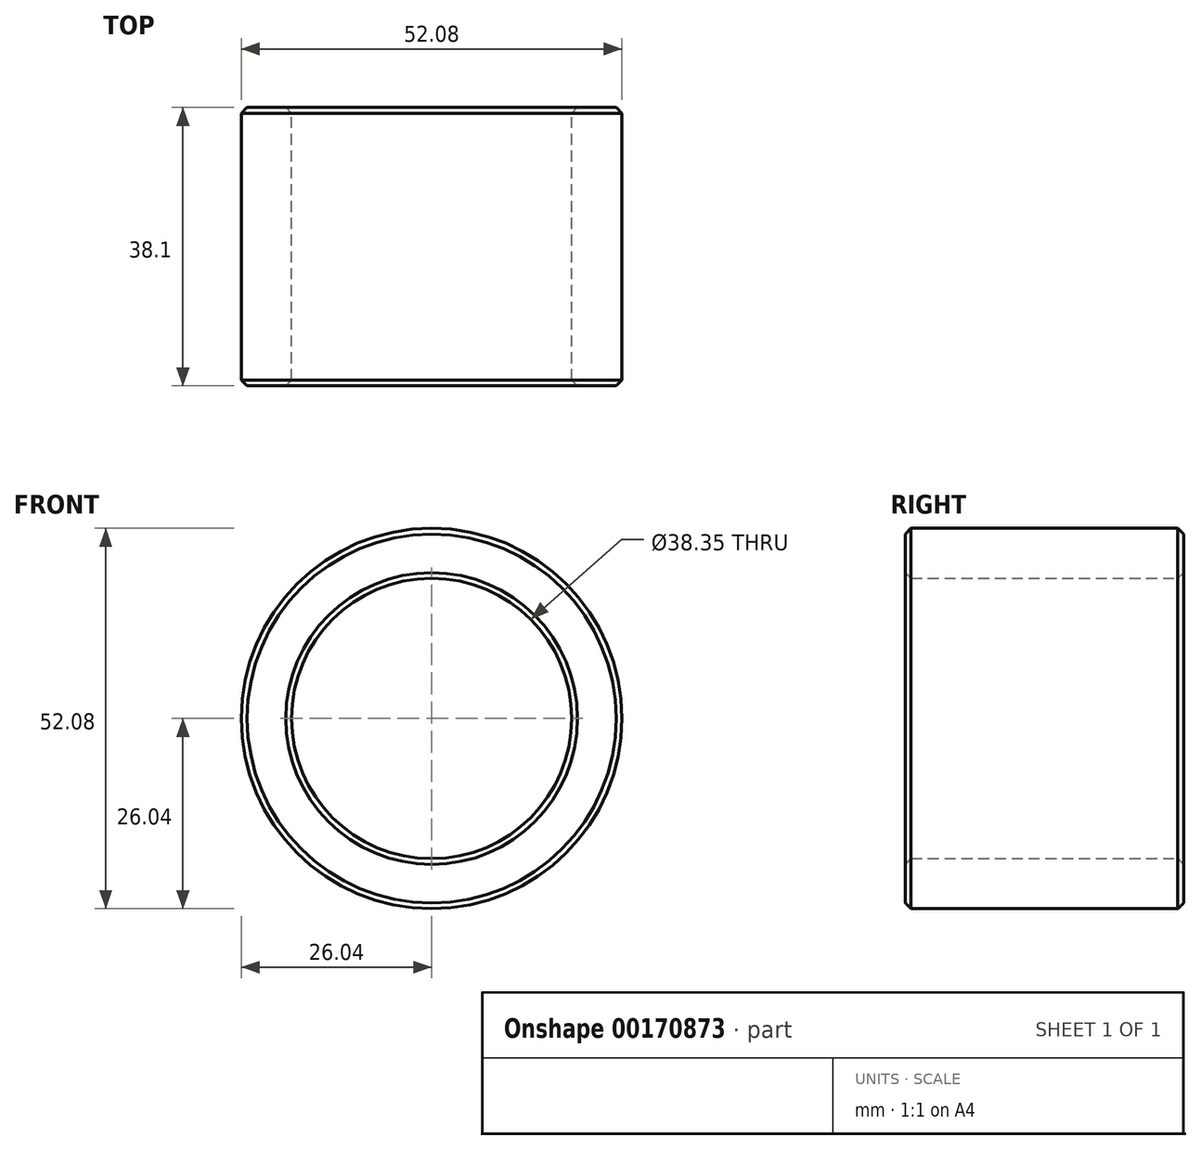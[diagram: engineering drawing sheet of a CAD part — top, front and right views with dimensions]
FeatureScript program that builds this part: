
annotation { "Feature Type Name" : "Feature", "Feature Type Description" : "" }
export const myFeature = defineFeature(function(context is Context, id is Id, definition is map)
    precondition{}
    {
        {
            var Q0;
            Q0=qCreatedBy(makeId("Front.planeOp"),FACE);
            var sketch = newSketch(context, id + "F0", { "sketchPlane" : qUnion([Q0])});
            skCircle(sketch, "E0", {"center": v(0, 0) * mm, "radius": 19.18 * mm});
            skCircle(sketch, "E1", {"center": v(0, 0) * mm, "radius": 26.04 * mm});
            skSolve(sketch);
        }
        {
            var Q0;
            Q0 = qSketchRegion(id + "F0", true);
            extrude(context, id + "F1", {"entities" : qUnion([Q0]), "depth" : 38.1 * mm});
        }
        {
            var Q0;
            Q0=makeQuery(id+"F1.opExtrude","CAP_EDGE",EDGE,{"disambiguationData":[OSD([sQuery(id+"F0.wireOp",EDGE,"E0")])],"isStart":false});
            var Q1;
            Q1=makeQuery(id+"F1.opExtrude","CAP_EDGE",EDGE,{"disambiguationData":[OSD([sQuery(id+"F0.wireOp",EDGE,"E1")])],"isStart":false});
            var Q2;
            Q2=makeQuery(id+"F1.opExtrude","CAP_EDGE",EDGE,{"disambiguationData":[OSD([sQuery(id+"F0.wireOp",EDGE,"E1")])],"isStart":true});
            var Q3;
            Q3=makeQuery(id+"F1.opExtrude","CAP_EDGE",EDGE,{"disambiguationData":[OSD([sQuery(id+"F0.wireOp",EDGE,"E0")])],"isStart":true});
            chamfer(context, id + "F2", {"entities" : qUnion([Q0, Q1, Q2, Q3]), "width" : 0.79 * mm, "tangentPropagation" : true});
        }
    });
